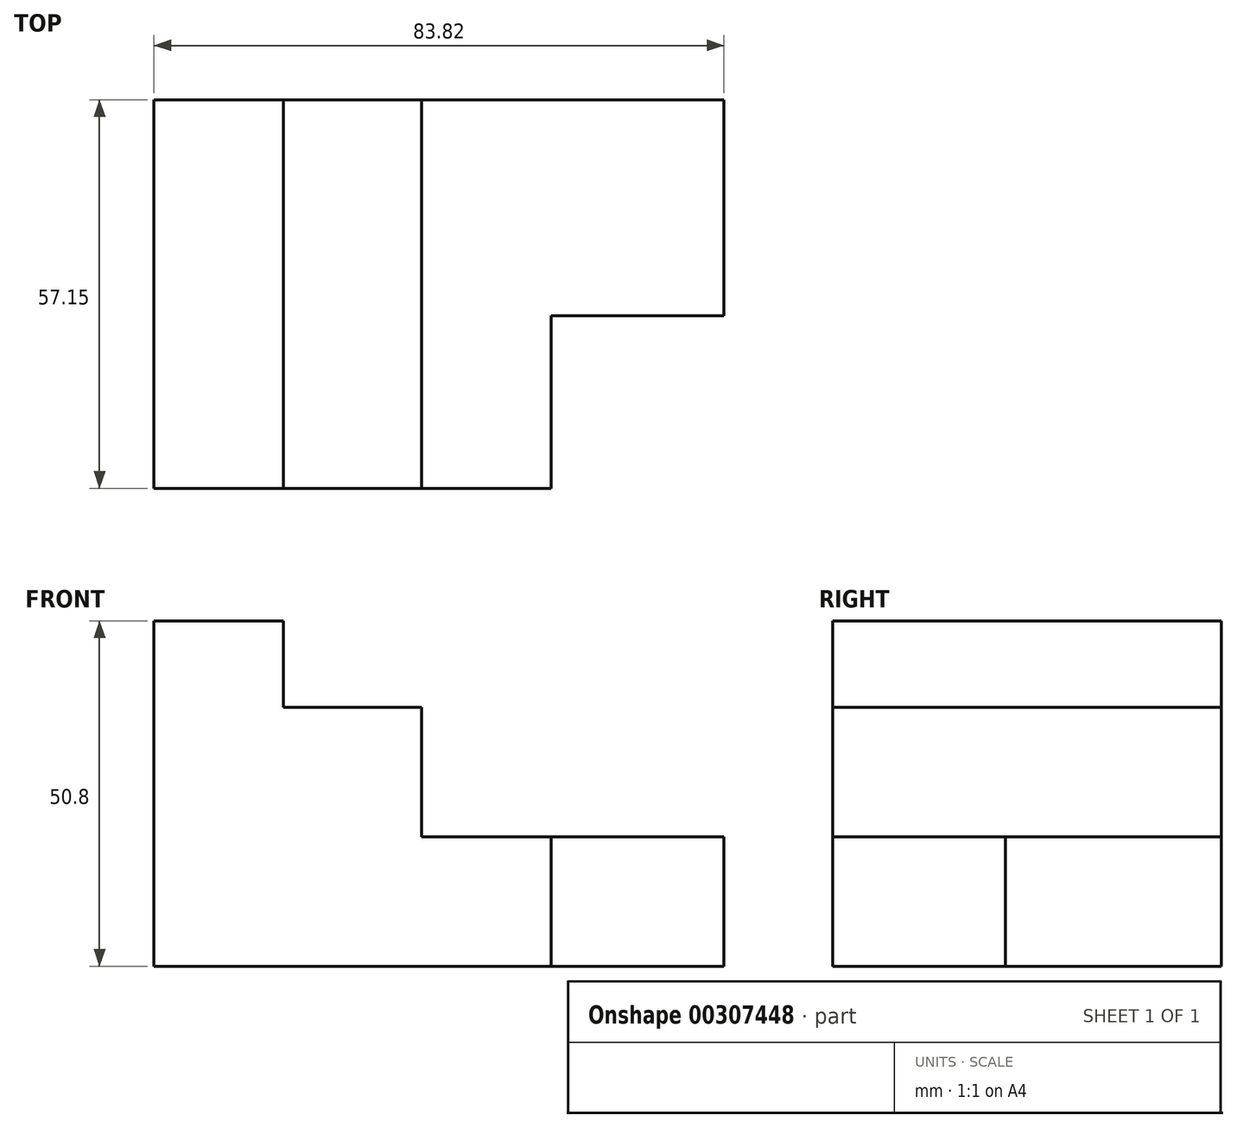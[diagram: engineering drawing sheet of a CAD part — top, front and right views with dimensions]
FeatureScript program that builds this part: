
annotation { "Feature Type Name" : "Feature", "Feature Type Description" : "" }
export const myFeature = defineFeature(function(context is Context, id is Id, definition is map)
    precondition{}
    {
        {
            var Q0;
            Q0=qCreatedBy(makeId("Front.planeOp"),FACE);
            var sketch = newSketch(context, id + "F0", { "sketchPlane" : qUnion([Q0])});
            skLineSegment(sketch, "E0", {"start": v(0, 0) * mm, "end": v(0, 50.8) * mm});
            skLineSegment(sketch, "E1", {"start": v(19.05, 50.8) * mm, "end": v(19.05, 38.1) * mm});
            skLineSegment(sketch, "E2", {"start": v(19.05, 38.1) * mm, "end": v(39.37, 38.1) * mm});
            skLineSegment(sketch, "E3", {"start": v(39.37, 38.1) * mm, "end": v(39.37, 19.05) * mm});
            skLineSegment(sketch, "E4", {"start": v(39.37, 19.05) * mm, "end": v(83.82, 19.05) * mm});
            skLineSegment(sketch, "E5", {"start": v(83.82, 19.05) * mm, "end": v(83.82, 0) * mm});
            skLineSegment(sketch, "E6", {"start": v(83.82, 0) * mm, "end": v(0, 0) * mm});
            skLineSegment(sketch, "E7", {"start": v(19.05, 50.8) * mm, "end": v(0, 50.8) * mm});
            skSolve(sketch);
        }
        {
            var Q0;
            Q0 = qSketchRegion(id + "F0", true);
            extrude(context, id + "F1", {"entities" : qUnion([Q0]), "depth" : 57.15 * mm});
        }
        {
            var Q0;
            Q0=makeQuery(id+"F1.opExtrude","SWEPT_FACE",FACE,{"disambiguationData":[OSD([sQuery(id+"F0.wireOp",EDGE,"E4")])]});
            var sketch = newSketch(context, id + "F2", { "sketchPlane" : qUnion([Q0])});
            skLineSegment(sketch, "E8.bottom", {"start": v(83.82, -57.15) * mm, "end": v(58.42, -57.15) * mm});
            skLineSegment(sketch, "E8.top", {"start": v(83.82, -31.75) * mm, "end": v(58.42, -31.75) * mm});
            skLineSegment(sketch, "E8.left", {"start": v(83.82, -57.15) * mm, "end": v(83.82, -31.75) * mm});
            skLineSegment(sketch, "E8.right", {"start": v(58.42, -57.15) * mm, "end": v(58.42, -31.75) * mm});
            skSolve(sketch);
        }
        {
            var Q0;
            Q0 = qSketchRegion(id + "F2", true);
            var Q1;
            Q1=makeQuery(id+"F1.opExtrude","SWEPT_FACE",FACE,{"disambiguationData":[OSD([sQuery(id+"F0.wireOp",EDGE,"E6")])]});
            extrude(context, id + "F3", {"entities" : qUnion([Q0]), "operationType" : NewBodyOperationType.REMOVE, "endBound" : BoundingType.UP_TO_SURFACE, "oppositeDirection" : true, "endBoundEntityFace" : qUnion([Q1]), "depth" : 25.4 * mm});
        }
    });
